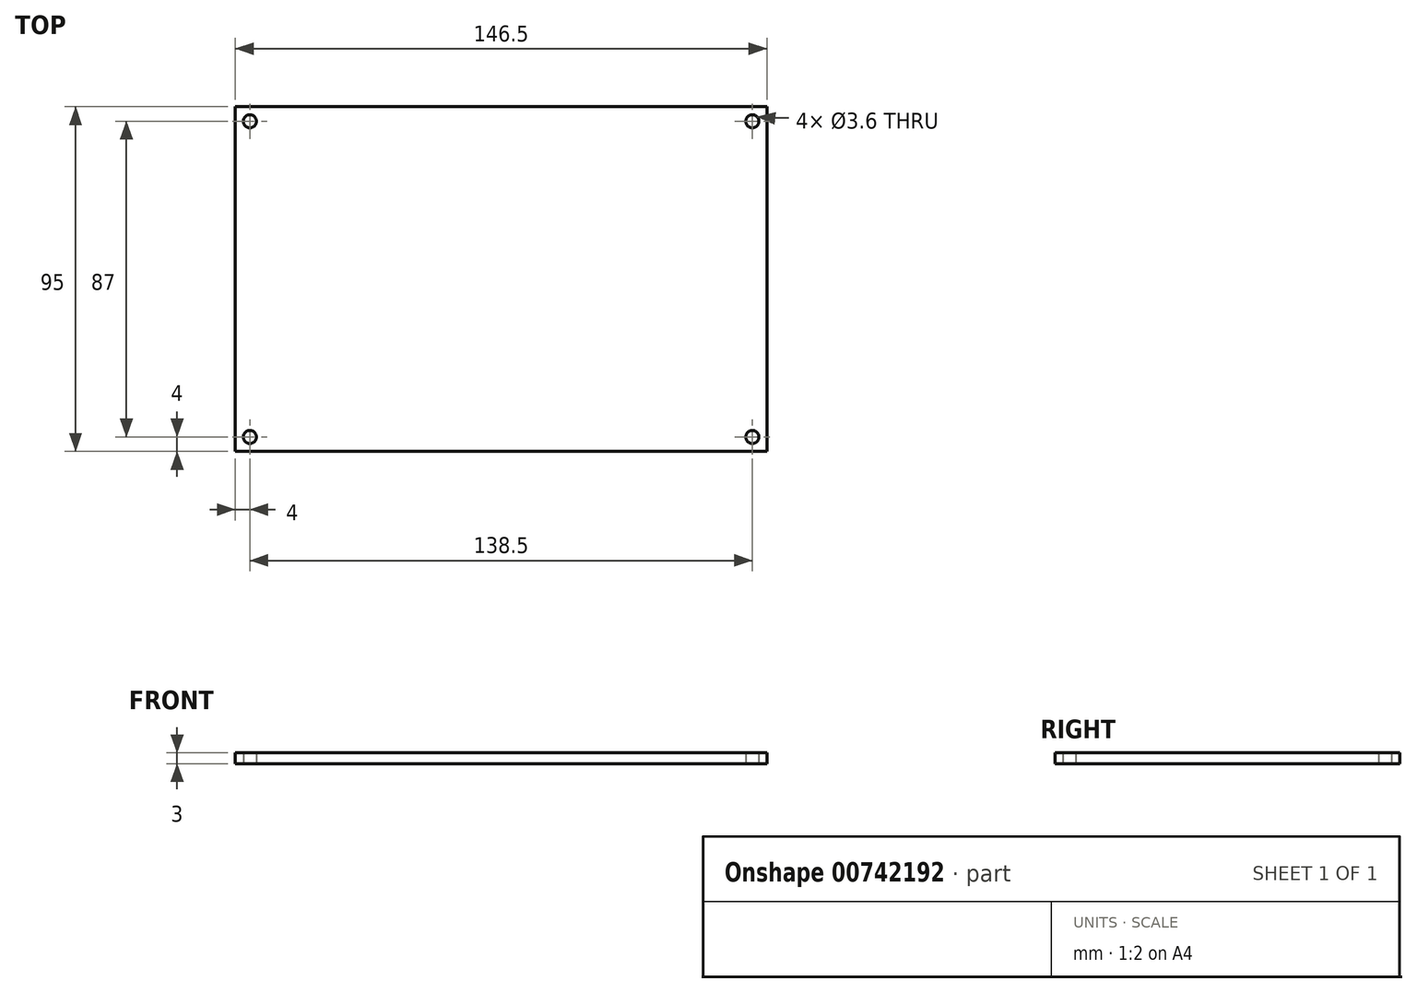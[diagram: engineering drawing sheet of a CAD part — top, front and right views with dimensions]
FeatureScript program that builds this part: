
annotation { "Feature Type Name" : "Feature", "Feature Type Description" : "" }
export const myFeature = defineFeature(function(context is Context, id is Id, definition is map)
    precondition{}
    {
        {
            var Q0;
            Q0=qCreatedBy(makeId("Top.planeOp"),FACE);
            var sketch = newSketch(context, id + "F0", { "sketchPlane" : qUnion([Q0])});
            skLineSegment(sketch, "E0.bottom", {"start": v(0, 0) * mm, "end": v(146.5, 0) * mm});
            skLineSegment(sketch, "E0.top", {"start": v(0, 95) * mm, "end": v(146.5, 95) * mm});
            skLineSegment(sketch, "E0.left", {"start": v(0, 0) * mm, "end": v(0, 95) * mm});
            skLineSegment(sketch, "E0.right", {"start": v(146.5, 0) * mm, "end": v(146.5, 95) * mm});
            skCircle(sketch, "E1", {"center": v(4, 91) * mm, "radius": 1.8 * mm});
            skLineSegment(sketch, "E2", {"start": v(0, 47.5) * mm, "end": v(146.5, 47.5) * mm, "construction": true});
            skLineSegment(sketch, "E3", {"start": v(73.25, 95) * mm, "end": v(73.25, 0) * mm, "construction": true});
            skCircle(sketch, "E4.MirrorC", {"center": v(4, 4) * mm, "radius": 1.8 * mm});
            skCircle(sketch, "E5.MirrorC", {"center": v(142.5, 91) * mm, "radius": 1.8 * mm});
            skCircle(sketch, "E6.MirrorC", {"center": v(142.5, 4) * mm, "radius": 1.8 * mm});
            skSolve(sketch);
        }
        {
            var Q0;
            Q0 = qSketchRegion(id + "F0", true);
            extrude(context, id + "F1", {"entities" : qUnion([Q0]), "depth" : 3 * mm, "offsetDistance" : 25 * mm});
        }
    });
